# Revit family: Sink_Undermount-American_Standard-Portsmouth-18SB.9232100S.075
name_source: partatom
category: Plumbing Fixtures
units: mm (PartAtom-declared; Revit-internal decimal feet)

## family parameters
Always vertical = No
Cut with Voids When Loaded = Yes
OmniClass Number = 23.45.05.14.14
OmniClass Title = Sinks/Lavatories
Part Type = Normal
Room Calculation Point = No
Round Connector Dimension = Use Diameter
Shared = Yes
Work Plane-Based = Yes

## types (1)
- 18SB.9232100S.075
    791676-100.0070A Undermount Sink Clips = No
    8449.232100D.075 Bottom grids = No
    9028000.075 Waste Fitting = Yes
    Assembly Code = D2010410
    Basin Shape = Rectangular
    Bottom Drain Outlet Length = 1"
    CW Connection = Yes
    CWFU = 2
    Cold Water Connection Diameter = 1/2"
    Cold Water Connection Height = 20"
    Cold Water Connection Radius = 1/4"
    Cold Water Connection Width = 4"
    Compliance Certifications = Meets or Exceeds the Following Specifications: • ASME A112.19.3
    Default Elevation = 0"
    Description = Portsmouth® 23 x 21-Inch Stainless Steel Undermount Single-Bowl Kitchen Sink
    Finish = Stainless Steel-American Standard-075-Satin
    HW Connection = Yes
    HWFU = 2
    Height = 9"
    Hot Water Connection Diameter = 1"
    Hot Water Connection Radius = 1/4"
    Hot Water Connection Width = 4"
    Installation Type = Undermount
    Length = 23 3/16"
    Manufacturer = American Standard
    Material = Stainless Steel-American Standard-075-Satin
    Model = 18SB.9232100S.075
    Price = Prices may vary. Please consult Manufacturer Representative for most up-to-date price list.
    Product Documentation Link = https://americanstandard.box.com
    Product Page URL = https://www.americanstandard-us.com
    Revised Date = 03/01/2023
    URL = https://www.americanstandard-us.com
    Vent Connection = No
    WFU = 3
    Wall Distance = 1 1/16"
    Warranty Information = Limited Lifetime Warranty
    Waste Connection = Yes
    Waste Connection Diameter = 1 1/2"
    Waste Connection Height = 18"
    Waste Connection Radius = 3/4"
    Width = 20 15/16"

## geometry (parser evidence)
native form markers: Sweep x4
no freeform markers — native parametric forms only
